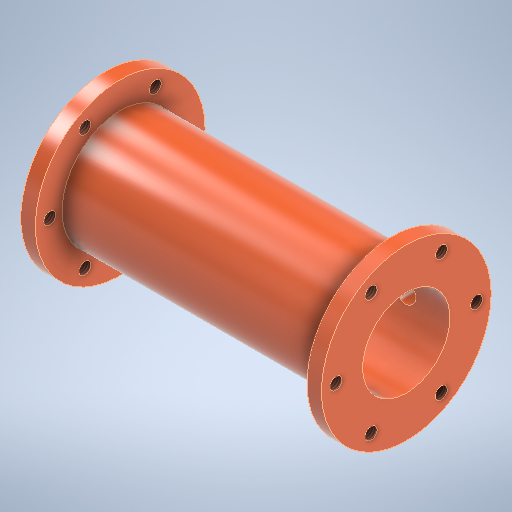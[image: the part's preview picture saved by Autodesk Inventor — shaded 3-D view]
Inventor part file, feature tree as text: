
AUTODESK INVENTOR PART (.ipt)
format: ipt  version: 2025.1 (Build 291241000, 241)  size: 372,736 bytes
history: native  units: mm
features: sketch x4, hole x3, plane x2, revolve x1, pattern_circular x1, mirror x1
ambient origin geometry x8: Origin, YZ Plane, XZ Plane, XY Plane, X Axis, Y Axis, Z Axis, Center Point
bodies: Solid1 (feature_tree)
feature tree (12):
  revolve  "Revolution1"  [1 undecoded]
  hole  "Hole1"  [1 undecoded]
  plane  "Work Plane1"
  hole  "Hole2"  [1 undecoded]
  pattern_circular  "Circular Pattern1"  [2 undecoded]
  mirror  "Mirror1"
  plane  "Work Plane3"
  hole  "Hole4"  [1 undecoded]
  sketch  "Sketch1"  dims[d0=24.0mm d1=35.0mm]
  sketch  "Sketch2"  dims[d2=3.0mm d3=3.0mm]
  sketch  "Sketch3"  dims[d4=56.0mm d5=90.0deg]
  sketch  "Sketch5"  dims[d6=18.0mm d7=6.0mm d8=4.0mm d9=2.0mm d10=90.0deg d11=8.0mm d12=20.594885mm d13=0.0mm d14=30.0deg d15=29.0mm d16=2.459mm d17=6.0mm d18=4.0mm d19=2.0mm d20=90.0deg d21=8.0mm d22=0.0mm d23=60.0mm d24=360.0deg d36=12.0mm d37=6.0mm d38=6.0mm d39=4.0mm d40=6.0mm d41=4.0mm d42=2.0mm d43=90.0deg d44=3.5mm d45=0.0mm]
note: 6 required parameter values undecoded (feature->parameter linkage not recoverable at this tier; creation-order binding heuristic only, values carry confidence <= 0.55)